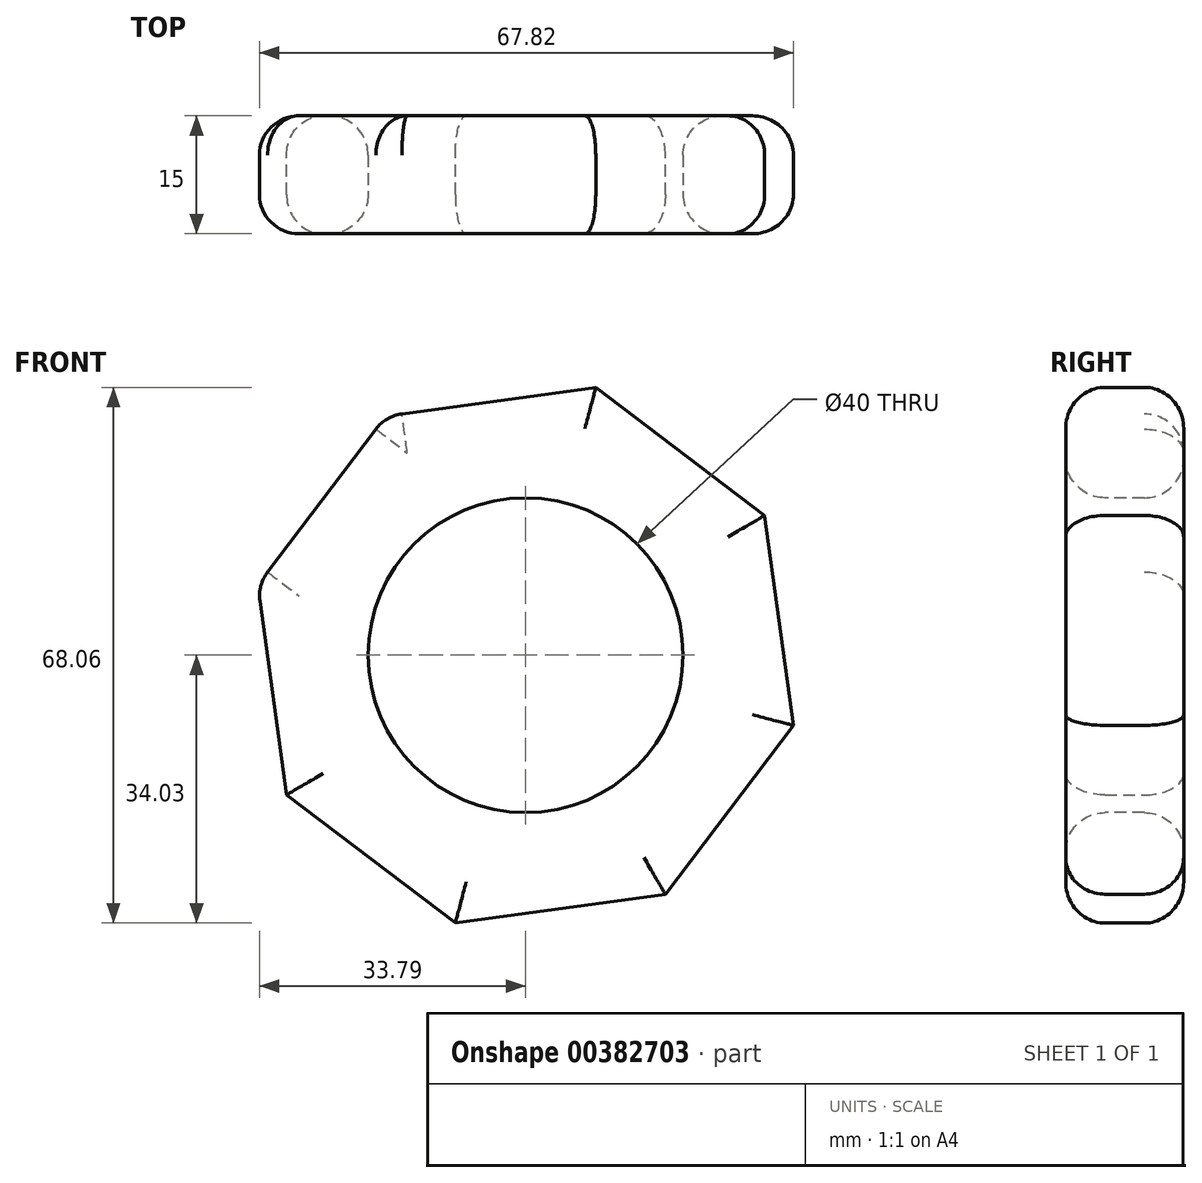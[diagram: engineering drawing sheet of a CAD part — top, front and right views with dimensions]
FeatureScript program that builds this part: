
annotation { "Feature Type Name" : "Feature", "Feature Type Description" : "" }
export const myFeature = defineFeature(function(context is Context, id is Id, definition is map)
    precondition{}
    {
        {
            var Q0;
            Q0=qCreatedBy(makeId("Front.planeOp"),FACE);
            var sketch = newSketch(context, id + "F0", { "sketchPlane" : qUnion([Q0])});
            skCircle(sketch, "E0.cCircle", {"center": v(0, 0) * mm, "radius": 32.5 * mm, "construction": true});
            skLineSegment(sketch, "E0.0", {"start": v(-34.03, 8.92) * mm, "end": v(-17.75, 30.37) * mm});
            skLineSegment(sketch, "E0.1", {"start": v(-17.75, 30.37) * mm, "end": v(8.92, 34.03) * mm});
            skLineSegment(sketch, "E0.2", {"start": v(8.92, 34.03) * mm, "end": v(30.37, 17.75) * mm});
            skLineSegment(sketch, "E0.3", {"start": v(30.37, 17.75) * mm, "end": v(34.03, -8.92) * mm});
            skLineSegment(sketch, "E0.4", {"start": v(34.03, -8.92) * mm, "end": v(17.75, -30.37) * mm});
            skLineSegment(sketch, "E0.5", {"start": v(17.75, -30.37) * mm, "end": v(-8.92, -34.03) * mm});
            skLineSegment(sketch, "E0.6", {"start": v(-8.92, -34.03) * mm, "end": v(-30.37, -17.75) * mm});
            skLineSegment(sketch, "E0.7", {"start": v(-30.37, -17.75) * mm, "end": v(-34.03, 8.92) * mm});
            skPoint(sketch, "E0.0.midPoint", {"position": v(-25.9, 19.64) * mm});
            skSolve(sketch);
        }
        {
            var Q0;
            Q0=makeQuery(id+"F0.imprint","IMPRINT",FACE,{"disambiguationData":[TD([[makeQuery(id+"F0.imprint","IMPRINT",EDGE,{"derivedFrom":sQuery(id+"F0.wireOp",EDGE,"E0.0")}),-1.0]])]});
            extrude(context, id + "F1", {"entities" : qUnion([Q0]), "depth" : 15 * mm});
        }
        {
            var Q0;
            Q0=makeQuery(id+"F1.opExtrude","CAP_FACE",FACE,{"disambiguationData":[OSD([sQuery(id+"F0.wireOp",EDGE,"E0.0"),sQuery(id+"F0.wireOp",EDGE,"E0.1"),sQuery(id+"F0.wireOp",EDGE,"E0.2"),sQuery(id+"F0.wireOp",EDGE,"E0.3"),sQuery(id+"F0.wireOp",EDGE,"E0.4"),sQuery(id+"F0.wireOp",EDGE,"E0.5"),sQuery(id+"F0.wireOp",EDGE,"E0.6"),sQuery(id+"F0.wireOp",EDGE,"E0.7")])],"isStart":false});
            var sketch = newSketch(context, id + "F2", { "sketchPlane" : qUnion([Q0])});
            skCircle(sketch, "E1", {"center": v(0, 0) * mm, "radius": 20 * mm});
            skSolve(sketch);
        }
        {
            var Q0;
            Q0=makeQuery(id+"F2.imprint","IMPRINT",FACE,{"disambiguationData":[TD([[makeQuery(id+"F2.imprint","IMPRINT",EDGE,{"derivedFrom":sQuery(id+"F2.wireOp",EDGE,"E1")}),1.0]])]});
            extrude(context, id + "F3", {"entities" : qUnion([Q0]), "operationType" : NewBodyOperationType.REMOVE, "oppositeDirection" : true, "depth" : 25 * mm});
        }
        {
            var Q0;
            Q0=makeQuery(id+"F1.opExtrude","CAP_FACE",FACE,{"disambiguationData":[OSD([sQuery(id+"F0.wireOp",EDGE,"E0.0"),sQuery(id+"F0.wireOp",EDGE,"E0.1"),sQuery(id+"F0.wireOp",EDGE,"E0.2"),sQuery(id+"F0.wireOp",EDGE,"E0.3"),sQuery(id+"F0.wireOp",EDGE,"E0.4"),sQuery(id+"F0.wireOp",EDGE,"E0.5"),sQuery(id+"F0.wireOp",EDGE,"E0.6"),sQuery(id+"F0.wireOp",EDGE,"E0.7")])],"isStart":false});
            var Q1;
            Q1=makeQuery(id+"F1.opExtrude","SWEPT_FACE",FACE,{"disambiguationData":[OSD([sQuery(id+"F0.wireOp",EDGE,"E0.0")])]});
            fillet(context, id + "F4", {"entities" : qUnion([Q0, Q1]), "radius" : 5 * mm, "tangentPropagation" : true, "allowEdgeOverflow" : false});
        }
        {
            var Q0;
            Q0=makeQuery(id+"F1.opExtrude","CAP_FACE",FACE,{"disambiguationData":[OSD([sQuery(id+"F0.wireOp",EDGE,"E0.0"),sQuery(id+"F0.wireOp",EDGE,"E0.1"),sQuery(id+"F0.wireOp",EDGE,"E0.2"),sQuery(id+"F0.wireOp",EDGE,"E0.3"),sQuery(id+"F0.wireOp",EDGE,"E0.4"),sQuery(id+"F0.wireOp",EDGE,"E0.5"),sQuery(id+"F0.wireOp",EDGE,"E0.6"),sQuery(id+"F0.wireOp",EDGE,"E0.7")])],"isStart":true});
            fillet(context, id + "F5", {"entities" : qUnion([Q0]), "radius" : 5 * mm, "tangentPropagation" : true, "allowEdgeOverflow" : false});
        }
    });
